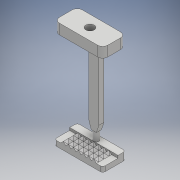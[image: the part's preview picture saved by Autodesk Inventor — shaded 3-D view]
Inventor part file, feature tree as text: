
AUTODESK INVENTOR PART (.ipt)
format: ipt  version: 2017 (Build 210142000, 142)  size: 247,296 bytes
history: native  units: mm
features: extrude x7, sketch x7, fillet x2, chamfer x2, projected_geometry x2
ambient origin geometry x8: Origin, YZ Plane, XZ Plane, XY Plane, X Axis, Y Axis, Z Axis, Center Point
bodies: Solid1 (feature_tree)
feature tree (20):
  extrude  "Extrusion1"  Depth=9.0mm
  extrude  "Extrusion2"  Depth=2.0mm
  extrude  "Extrusion5"  Depth=3.5mm TaperAngle=0.0deg
  extrude  "Extrusion6"  Depth=32.0mm TaperAngle=0.0deg
  extrude  "Extrusion7"  Depth=4.0mm
  extrude  "Extrusion8"  Depth=1.0mm
  extrude  "Extrusion9"  TaperAngle=135.0deg  [1 undecoded]
  fillet  "Fillet2"  [1 undecoded]
  fillet  "Fillet3"  Radius=4.0mm
  chamfer  "Chamfer1"  Angle=135.0deg  [1 undecoded]
  chamfer  "Chamfer2"  Distance=2.0mm
  sketch  "Sketch1"  dims[d0=19.0mm d1=9.0mm]
  sketch  "Sketch2"  dims[d2=3.0mm d3=0.0mm d4=2.0mm]
  sketch  "Sketch6"  dims[d5=2.0mm d6=3.5mm d7=0.0mm]
  sketch  "Sketch7"  dims[d13=4.0mm d14=32.0mm d15=0.0mm]
  projected_geometry  "Projected Loop2"
  sketch  "Sketch8"  dims[d16=4.0mm d17=0.0mm d18=3.3mm]
  projected_geometry  "Projected Loop3"
  sketch  "Sketch10"  dims[d19=4.0mm d20=0.0mm d23=1.0mm]
  sketch  "Sketch11"  dims[d24=6.0mm d25=135.0deg d26=90.0deg d27=4.0mm d28=0.0mm d30=135.0deg d31=40.0mm d33=2.0mm d34=10.0mm d36=10.0mm d38=40.0mm d40=2.0mm d41=10.0mm d43=10.0mm d45=6.0mm d46=0.0mm d47=1.0mm d48=2.0mm d49=1.0mm d50=3.0mm d51=45.0deg d52=1.0mm d53=3.0mm d54=45.0deg]
note: 3 required parameter values undecoded (feature->parameter linkage not recoverable at this tier; creation-order binding heuristic only, values carry confidence <= 0.55)
